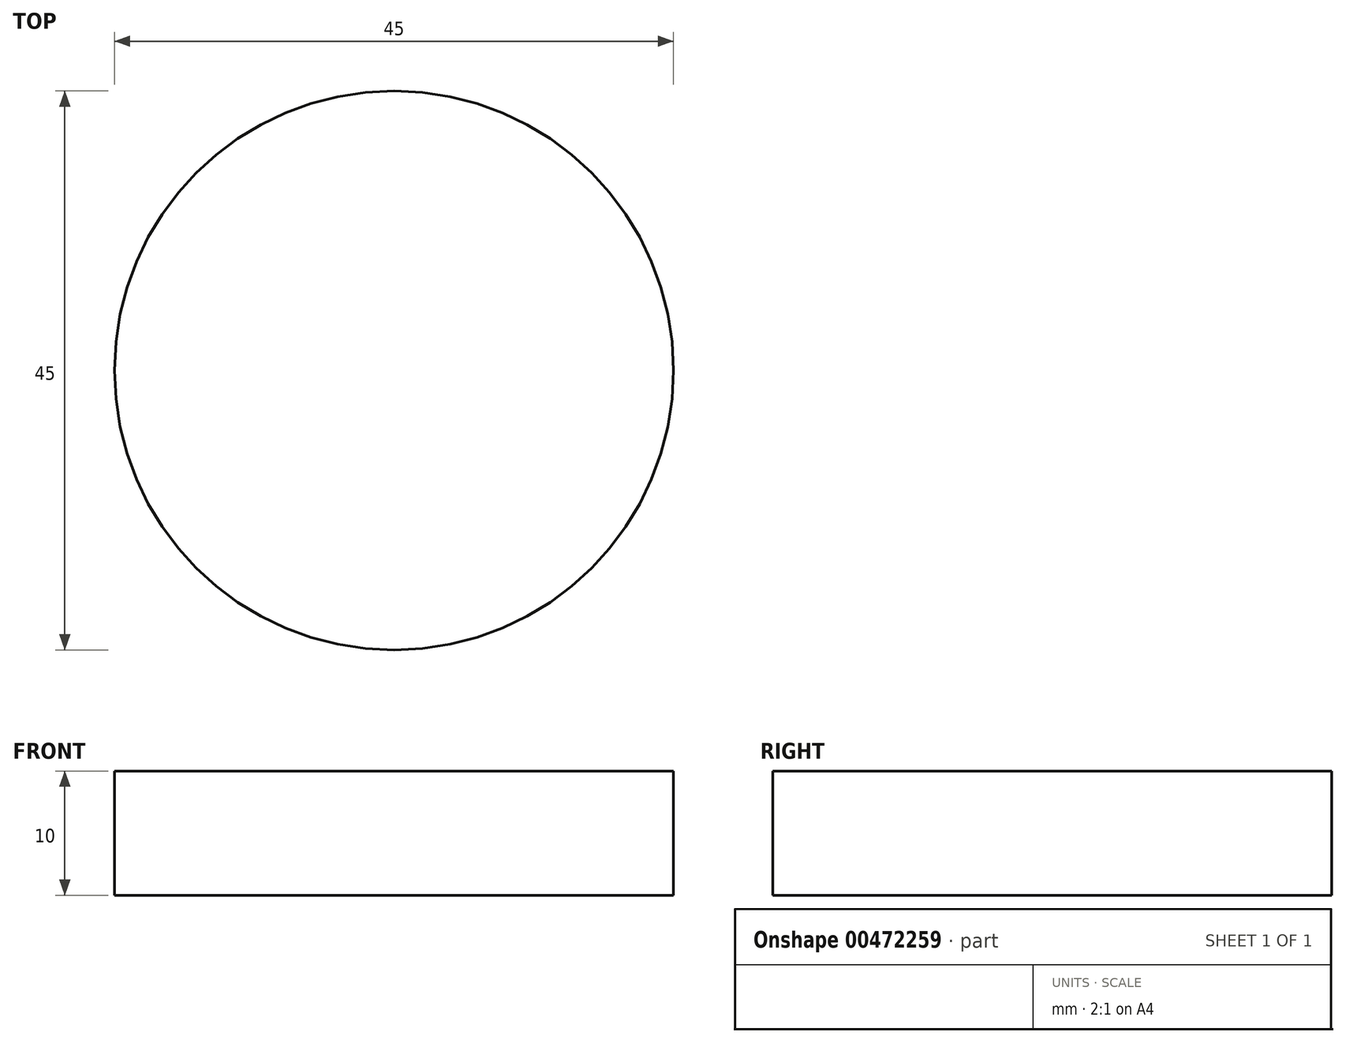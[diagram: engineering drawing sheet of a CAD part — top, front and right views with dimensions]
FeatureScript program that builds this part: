
annotation { "Feature Type Name" : "Feature", "Feature Type Description" : "" }
export const myFeature = defineFeature(function(context is Context, id is Id, definition is map)
    precondition{}
    {
        {
            var Q0;
            Q0=qCreatedBy(makeId("Top.planeOp"),FACE);
            var sketch = newSketch(context, id + "F0", { "sketchPlane" : qUnion([Q0])});
            skCircle(sketch, "E0", {"center": v(-19.54, 11.25) * mm, "radius": 22.5 * mm});
            skSolve(sketch);
        }
        {
            var Q0;
            Q0 = qSketchRegion(id + "F0", true);
            extrude(context, id + "F1", {"entities" : qUnion([Q0]), "depth" : 10 * mm});
        }
        {
            var Q0;
            Q0=qCreatedBy(makeId("Top.planeOp"),FACE);
            var sketch = newSketch(context, id + "F2", { "sketchPlane" : qUnion([Q0])});
            skCircle(sketch, "E1", {"center": v(-19.54, 11.25) * mm, "radius": 22.5 * mm});
            skSolve(sketch);
        }
        {
            var Q0;
            Q0 = qConstructionFilter(qBodyType(qCreatedBy(id + "F2" ,EDGE), BodyType.WIRE), ConstructionObject.NO);
            extrude(context, id + "F3", {"bodyType" : ToolBodyType.SURFACE, "surfaceEntities" : qUnion([Q0]), "depth" : 50 * mm});
        }
    });
